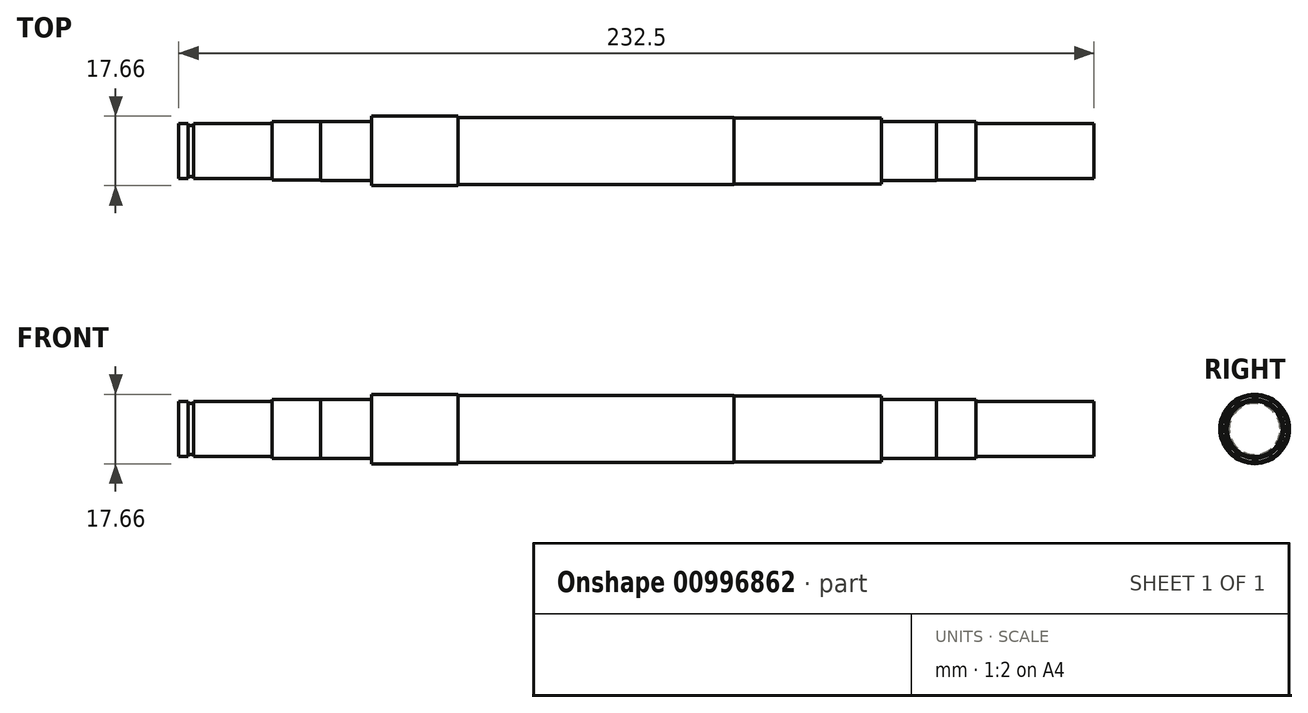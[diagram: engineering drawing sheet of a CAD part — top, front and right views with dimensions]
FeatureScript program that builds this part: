
annotation { "Feature Type Name" : "Feature", "Feature Type Description" : "" }
export const myFeature = defineFeature(function(context is Context, id is Id, definition is map)
    precondition{}
    {
        {
            var Q0;
            Q0=qCreatedBy(makeId("Front.planeOp"),FACE);
            var sketch = newSketch(context, id + "F0", { "sketchPlane" : qUnion([Q0])});
            skLineSegment(sketch, "E0", {"start": v(-120, 0) * mm, "end": v(120, 0) * mm, "construction": true});
            skLineSegment(sketch, "E1", {"start": v(-116, 0) * mm, "end": v(-116, 7) * mm});
            skLineSegment(sketch, "E2", {"start": v(-116, 7) * mm, "end": v(-113.6, 7) * mm});
            skLineSegment(sketch, "E3", {"start": v(-113.6, 7) * mm, "end": v(-113.6, 6.5) * mm});
            skLineSegment(sketch, "E4", {"start": v(-113.6, 6.5) * mm, "end": v(-112.3, 6.5) * mm});
            skLineSegment(sketch, "E5", {"start": v(-112.3, 6.5) * mm, "end": v(-112.3, 7) * mm});
            skLineSegment(sketch, "E6", {"start": v(-112.3, 7) * mm, "end": v(-92.3, 7) * mm});
            skLineSegment(sketch, "E7", {"start": v(-92.3, 7) * mm, "end": v(-92.3, 7.45) * mm});
            skLineSegment(sketch, "E8", {"start": v(-92.3, 7.45) * mm, "end": v(-80, 7.45) * mm});
            skLineSegment(sketch, "E9", {"start": v(-80, 7.45) * mm, "end": v(-80, 7.5) * mm});
            skLineSegment(sketch, "E10", {"start": v(-80, 7.5) * mm, "end": v(-67, 7.5) * mm});
            skLineSegment(sketch, "E11", {"start": v(-67, 7.5) * mm, "end": v(-67, 8.82) * mm});
            skLineSegment(sketch, "E12", {"start": v(-67, 8.82) * mm, "end": v(-45, 8.82) * mm});
            skLineSegment(sketch, "E13", {"start": v(-45, 8.82) * mm, "end": v(-45, 8.5) * mm});
            skLineSegment(sketch, "E14", {"start": v(62.5, 8.38) * mm, "end": v(62.5, 7.5) * mm});
            skLineSegment(sketch, "E15", {"start": v(62.5, 7.5) * mm, "end": v(76.5, 7.5) * mm});
            skLineSegment(sketch, "E16", {"start": v(76.5, 7.5) * mm, "end": v(76.5, 7.45) * mm});
            skLineSegment(sketch, "E17", {"start": v(76.5, 7.45) * mm, "end": v(86.5, 7.45) * mm});
            skLineSegment(sketch, "E18", {"start": v(86.5, 7.45) * mm, "end": v(86.5, 7) * mm});
            skPoint(sketch, "E18.endSnap0", {"position": v(-102.3, 7) * mm});
            skLineSegment(sketch, "E19", {"start": v(86.5, 7) * mm, "end": v(116.5, 7) * mm});
            skLineSegment(sketch, "E20", {"start": v(116.5, 7) * mm, "end": v(116.5, 0) * mm});
            skLineSegment(sketch, "E21", {"start": v(62.5, 8.38) * mm, "end": v(25, 8.38) * mm});
            skLineSegment(sketch, "E22", {"start": v(25, 8.38) * mm, "end": v(25, 8.5) * mm});
            skLineSegment(sketch, "E23", {"start": v(-45, 8.5) * mm, "end": v(25, 8.5) * mm});
            skLineSegment(sketch, "E24", {"start": v(-116, 0) * mm, "end": v(116.5, 0) * mm});
            skSolve(sketch);
        }
        {
            var Q0;
            Q0 = qSketchRegion(id + "F0", true);
            var Q1;
            Q1=sQuery(id+"F0.wireOp",EDGE,"E0");
            revolve(context, id + "F1", {"surfaceOperationType" : NewSurfaceOperationType.NEW, "entities" : qUnion([Q0]), "axis" : qUnion([Q1]), "revolveType" : RevolveType.FULL});
        }
    });
